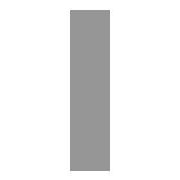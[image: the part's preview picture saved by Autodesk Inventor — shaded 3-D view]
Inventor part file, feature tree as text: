
AUTODESK INVENTOR PART (.ipt)
format: ipt  version: 2024 (Build 280153000, 153)  size: 117,248 bytes
history: native  units: mm (DEFAULTED — no unit token found)
features: other x4, sketch x3, hole x2, plane x1
ambient origin geometry x8: Origin, YZ Plane, XZ Plane, XY Plane, X Axis, Y Axis, Z Axis, Center Point
bodies: Solid1 (feature_tree), Body (feature_tree)
feature tree (10):
  parser-record x1  (decoder bookkeeping rows leaked as tree rows — omitted from the tree; the rows remain in map.json)
  other  "Driven Length"
  other  "Start Plane"
  other  "End Plane"
  hole  "Hole1"  [1 undecoded]
  hole  "Hole2"  [1 undecoded]
  sketch  "Sketch3"  dims[d0=200.0mm d1=15.0mm]
  plane  "Work Plane3"
  sketch  "Sketch5"  dims[d2=475.0mm d3=0.0mm]
  sketch  "Sketch6"  dims[d4=7.5mm d5=100.0mm d6=-0.0mm d7=475.0mm d8=90.0deg d9=475.0mm d10=17.5mm d11=6.0mm d12=4.0mm d13=2.0mm d14=90.0deg d15=8.0mm d16=0.0mm d17=17.5mm d18=6.0mm d19=4.0mm d20=2.0mm d21=90.0deg d22=8.0mm d23=0.0mm]
note: 2 required parameter values undecoded (feature->parameter linkage not recoverable at this tier; creation-order binding heuristic only, values carry confidence <= 0.55)
